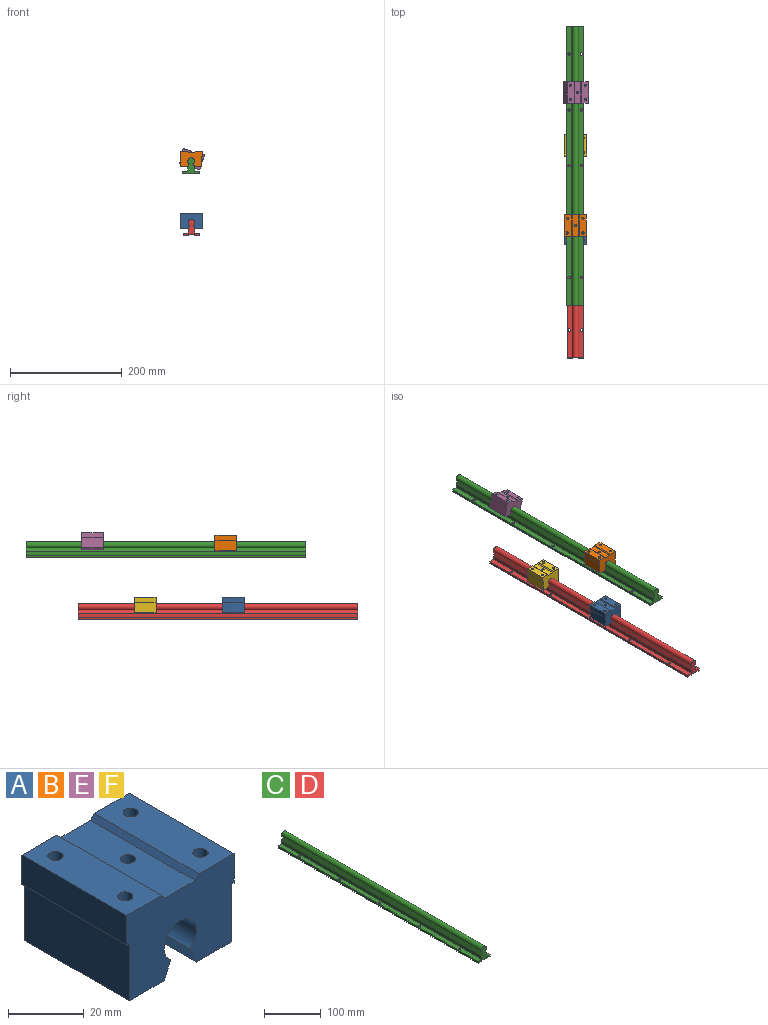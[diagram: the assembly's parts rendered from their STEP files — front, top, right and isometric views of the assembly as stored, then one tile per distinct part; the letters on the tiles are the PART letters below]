
ASSEMBLY  parts=6 mates=7
PART A: 27 faces, bbox 40x39x28 mm
  f0: plane 39x13.04mm, normal (0,0,-1), area 508.4mm2, adj f1,f2,f21,f24
  f1: plane 40x28mm, normal (0,-1,0), area 904.2mm2, adj f0,f3,f4,f5,f6,f7,f16,f17
  f2: plane 40x28mm, normal (0,1,0), area 904.2mm2, adj f0,f3,f4,f5,f6,f7,f16,f17
  f3: plane 39x13.04mm, normal (0,0,-1), area 508.4mm2, adj f1,f2,f22,f25
  f4: plane 39x13mm, normal (0,0,1), area 481.9mm2, adj f1,f2,f6,f10,f12,f16
  f5: plane 39x9.5mm, normal (-1,0,0), area 370.5mm2, adj f1,f2,f7,f23
  f6: plane 39x9.5mm, normal (1,0,0), area 370.5mm2, adj f1,f2,f4,f20
  f7: plane 39x13mm, normal (0,0,1), area 481.9mm2, adj f1,f2,f5,f8,f14,f17
  f8: cylinder r=2mm len=15mm, axis (0,0,1), area 188.5mm2, adj f7,f9
  f9: plane 4x4mm, normal (0,0,1), area 12.6mm2, adj f8
  f10: cylinder r=2mm len=15mm, axis (0,0,1), area 188.5mm2, adj f4,f11
  f11: plane 4x4mm, normal (0,0,1), area 12.6mm2, adj f10
  f12: cylinder r=2mm len=15mm, axis (0,0,1), area 188.5mm2, adj f4,f13
  f13: plane 4x4mm, normal (0,0,1), area 12.6mm2, adj f12
  f14: cylinder r=2mm len=15mm, axis (0,0,1), area 188.5mm2, adj f7,f15
  f15: plane 4x4mm, normal (0,0,1), area 12.6mm2, adj f14
  f16: plane 39x1.5mm, normal (-0.71,0,0.71), area 82.7mm2, adj f1,f2,f4,f18
  f17: plane 39x1.5mm, normal (0.71,0,0.71), area 82.7mm2, adj f1,f2,f7,f18
  f18: plane 39x11mm, normal (0,0,1), area 416.4mm2, adj f1,f2,f16,f17,f19
  f19: cylinder r=2mm len=10.44mm, axis (0,0,1), area 129.1mm2, adj f18,f26
  f20: plane 39x1mm, normal (0,0,-1), area 39mm2, adj f1,f2,f6,f21
  f21: plane 39x18.5mm, normal (1,0,0), area 721.5mm2, adj f0,f1,f2,f20
  f22: plane 39x18.5mm, normal (-1,0,0), area 721.5mm2, adj f1,f2,f3,f23
  f23: plane 39x1mm, normal (0,0,-1), area 39mm2, adj f1,f2,f5,f22
  f24: plane 39x5.53mm, normal (-0.91,0,-0.41), area 236mm2, adj f0,f1,f2,f26
  f25: plane 39x5.53mm, normal (0.91,0,-0.41), area 236mm2, adj f1,f2,f3,f26
  f26: cylinder r=6mm len=39mm, axis (0,-1,0), area 1166mm2, adj f1,f2,f19,f24,f25
PART B: same geometry as A
PART C: 26 faces, bbox 30x500x28.4 mm
  f0: cylinder r=6mm len=500mm, axis (0,1,0), area 15492.1mm2, adj f1,f13,f14,f15
  f1: plane 500x6.32mm, normal (-0.91,0,0.41), area 3457.1mm2, adj f0,f2,f14,f15
  f2: plane 500x7mm, normal (-1,0,0), area 3500mm2, adj f1,f3,f14,f15
  f3: plane 500x9mm, normal (0,0,1), area 4427.4mm2, adj f2,f4,f14,f15,f21,f22,f23,f24
  f4: plane 500x4mm, normal (-1,0,0), area 2000mm2, adj f3,f5,f14,f15
  f5: plane 500x9.35mm, normal (0,0,-1), area 4602.4mm2, adj f4,f6,f14,f15,f21,f22,f23,f24
  f6: plane 500x1mm, normal (1,0,0), area 500mm2, adj f5,f7,f14,f15
  f7: plane 500x11.3mm, normal (0,0,-1), area 5650mm2, adj f6,f8,f14,f15
  f8: plane 500x1mm, normal (-1,0,0), area 500mm2, adj f7,f9,f14,f15
  f9: plane 500x9.35mm, normal (0,0,-1), area 4602.4mm2, adj f8,f10,f14,f15,f16,f17,f18,f19
  f10: plane 500x4mm, normal (1,0,0), area 2000mm2, adj f9,f11,f14,f15
  f11: plane 500x9mm, normal (0,0,1), area 4427.4mm2, adj f10,f12,f14,f15,f16,f17,f18,f19
  f12: plane 500x7mm, normal (1,0,0), area 3500mm2, adj f11,f13,f14,f15
  f13: plane 500x6.32mm, normal (0.91,0,0.41), area 3457.1mm2, adj f0,f12,f14,f15
  f14: plane 30x28.4mm, normal (0,-1,0), area 359.9mm2, adj f0,f1,f2,f3,f4,f5,f6,f7
  f15: plane 30x28.4mm, normal (0,1,0), area 359.9mm2, adj f0,f1,f2,f3,f4,f5,f6,f7
  f16: cylinder r=2.15mm len=4.3mm, axis (0,0,1), area 54mm2, adj f9,f11
  f17: cylinder r=2.15mm len=4.3mm, axis (0,0,1), area 54mm2, adj f9,f11
  f18: cylinder r=2.15mm len=4.3mm, axis (0,0,1), area 54mm2, adj f9,f11
  f19: cylinder r=2.15mm len=4.3mm, axis (0,0,1), area 54mm2, adj f9,f11
  f20: cylinder r=2.15mm len=4.3mm, axis (0,0,1), area 54mm2, adj f9,f11
  f21: cylinder r=2.15mm len=4.3mm, axis (0,0,1), area 54mm2, adj f3,f5
  f22: cylinder r=2.15mm len=4.3mm, axis (0,0,1), area 54mm2, adj f3,f5
  f23: cylinder r=2.15mm len=4.3mm, axis (0,0,1), area 54mm2, adj f3,f5
  f24: cylinder r=2.15mm len=4.3mm, axis (0,0,1), area 54mm2, adj f3,f5
  f25: cylinder r=2.15mm len=4.3mm, axis (0,0,1), area 54mm2, adj f3,f5
PART D: same geometry as C
PART E: same geometry as A
PART F: same geometry as A
PLACE A t=(47.56,-130.48,-83.57)mm
PLACE B t=(46.99,-116.95,26.8)mm
PLACE C t=(46.99,220.82,26.8)mm fixed
PLACE D t=(47.56,127.2,-83.57)mm fixed
PLACE E rot(axis=(0,1,0),15.9deg) t=(46.99,121.51,26.8)mm
PLACE F t=(47.56,27.32,-83.57)mm
MATE cylindrical A.f26 <-> D.f0  axis (0,-1,0) through (47.56,-169.48,-83.57)mm
MATE cylindrical B.f26 <-> C.f0  axis (0,1,0) through (46.99,-116.95,26.8)mm
MATE parallel C.f3 <-> B.f3  axis (0,0,1) through (36.5,-29.18,8.4)mm
MATE cylindrical D.f0 <-> F.f26  axis (0,-1,0) through (47.56,-372.8,-83.57)mm
MATE cylindrical E.f26 <-> C.f0  axis (0,1,0) through (46.99,121.51,26.8)mm
MATE parallel A.f0 <-> D.f11  axis (0,0,-1) through (60.04,-149.98,-93.97)mm
MATE parallel F.f0 <-> D.f11  axis (0,0,-1) through (66.56,-11.68,-93.97)mm
